# Revit family: Haworth_Intuity_Benching_Corner120_SingleSided
name_source: partatom
category: Furniture Systems
revit_build: Autodesk Revit 2018 (Build: 20170223_1515(x64)
units: mm (PartAtom-declared; Revit-internal decimal feet)

## family parameters
Always vertical = Yes
Cut with Voids When Loaded = No
OmniClass Number = 23.40.70.14.64.21
OmniClass Title = Systems Furniture
Part Type = Normal
Room Calculation Point = No
Round Connector Dimension = Use Diameter
Shared = No
Work Plane-Based = No

## types (6) — shared parameters
Accent Plate Finish = Haworth _ Paint _ Metallic Silver
Access Hatch Finish = Haworth _ Paint _ Metallic Silver
Access Plate Depth = 4 1/4"
Access Plate Height = 3/8"
Access Plate Offset = 7/8"
Actual Height = 29 3/16"
Assembly Code = E2020200
Back Leg Offset = 1 7/8"
Beam Depth = 1 1/4"
Beam Gap = 9/16"
Beam Height = 2"
Beam Offset = 7"
Custom Size = No
Description = Haworth - Intuity Benching - 120 Single Sided
End Cap Depth Half = 1 13/32"
End Cap Offset = 1/8"
Leg Finish = Haworth _ Paint _ Metallic Silver
Leg Half = 1"
Leg Height = 28"
Manufacturer = Haworth
Max Screen Width = 54"
Max Width = 54"
Min Screen Width = 36"
Min Width = 42"
Model = Intuity
Rail Finish = Haworth _ Paint _ Metallic Silver
Revision Number = 1
Screen Finish = Haworth _ Fabric _ Tellure _ Geranium 3A-42
Size = Verify Final Dim. w/ Haworth
Standard Bench Widths = 42, 48, 54 in
Standard Screen Widths = 42, 48, 54 in
Sustainability Info = http://www.haworth.com
Top Thickness = 1 3/16"
URL = www.haworth.com
URL - Product = http://www.haworth.com
Utility Tray Bottom = 21 23/64"
Utility Tray Offset = 1 9/32"
Warranty = http://www.haworth.com
Worksurface Edge Finish = Haworth _ Laminate _ Linen H-WL
Worksurface Finish = Haworth _ Laminate _ Linen H-WL

## per-type parameters (varying)
| type | 24 Depth | 30 Depth | Actual Depth | Actual Screen Width | Actual Width | Actual Worksurface Depth | Custom Screen Size | Half Width | Screen Width | Width | Worksurface Depth |
| 30d 54w | No | Yes | 31 13/32" | 53 3/4" | 54" | 30" | Yes | 27" | 54" | 54" | 30" |
| 30d 48w | No | Yes | 31 13/32" | 47 3/4" | 48" | 30" | No | 24" | 48" | 48" | 30" |
| 30d 42w | No | Yes | 31 13/32" | 41 3/4" | 42" | 30" | No | 21" | 42" | 42" | 30" |
| 24d 42w | Yes | No | 25 13/32" | 41 3/4" | 42" | 24" | No | 21" | 42" | 42" | 24" |
| 24d 48w | Yes | No | 25 13/32" | 47 3/4" | 48" | 24" | No | 24" | 48" | 48" | 24" |
| 24d 54w | Yes | No | 25 13/32" | 53 3/4" | 54" | 24" | Yes | 27" | 54" | 54" | 24" |

## geometry (parser evidence)
native form markers: Sweep x22
no freeform markers — native parametric forms only
